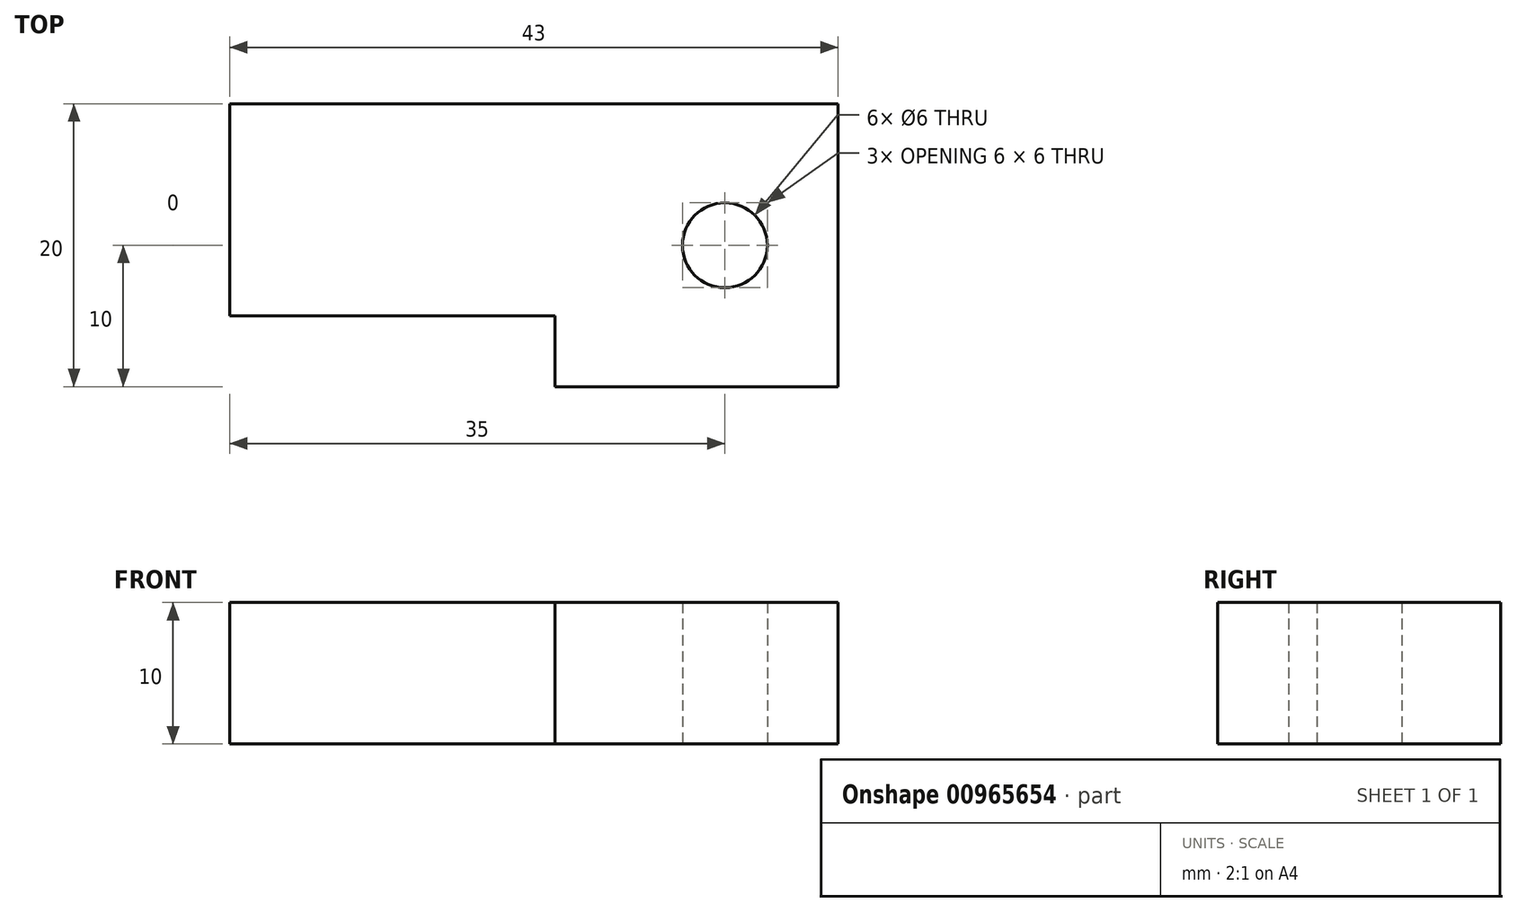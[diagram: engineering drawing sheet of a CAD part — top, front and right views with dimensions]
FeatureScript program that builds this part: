
annotation { "Feature Type Name" : "Feature", "Feature Type Description" : "" }
export const myFeature = defineFeature(function(context is Context, id is Id, definition is map)
    precondition{}
    {
        {
            var Q0;
            Q0=qCreatedBy(makeId("Top.planeOp"),FACE);
            var sketch = newSketch(context, id + "F0", { "sketchPlane" : qUnion([Q0])});
            skLineSegment(sketch, "E0.bottom", {"start": v(21.5, -10) * mm, "end": v(-21.5, -10) * mm});
            skLineSegment(sketch, "E0.top", {"start": v(21.5, 10) * mm, "end": v(-21.5, 10) * mm});
            skLineSegment(sketch, "E0.left", {"start": v(21.5, -10) * mm, "end": v(21.5, 10) * mm});
            skLineSegment(sketch, "E0.right", {"start": v(-21.5, -10) * mm, "end": v(-21.5, 10) * mm});
            skPoint(sketch, "E0.middle", {"position": v(0, 0) * mm});
            skPoint(sketch, "E1.centerSnap0", {"position": v(21.5, 0) * mm});
            skPoint(sketch, "E2", {"position": v(13.5, 0) * mm});
            skSolve(sketch);
        }
        {
            var Q0;
            Q0 = qSketchRegion(id + "F0", true);
            extrude(context, id + "F1", {"entities" : qUnion([Q0]), "depth" : 10 * mm, "offsetDistance" : 25 * mm});
        }
        {
            var Q0;
            Q0=sQuery(id+"F0.wireOp",VERTEX,"E2");
            var Q1;
            Q1=makeQuery(id+"F1.opExtrude","SWEPT_BODY",BODY,{"disambiguationData":[OSD([sQuery(id+"F0.wireOp",EDGE,"E0.bottom"),sQuery(id+"F0.wireOp",EDGE,"E0.top"),sQuery(id+"F0.wireOp",EDGE,"E0.left"),sQuery(id+"F0.wireOp",EDGE,"E0.right")])]});
            hole(context, id + "F2", {"style" : HoleStyle.SIMPLE, "endStyle" : HoleEndStyle.THROUGH, "oppositeDirection" : true, "holeDiameter" : 6 * mm, "majorDiameter" : 5 * mm, "isTappedThrough" : true, "tappedDepth" : 12 * mm, "tapClearance" : 3, "locations" : qUnion([Q0]), "scope" : qUnion([Q1])});
        }
        {
            var Q0;
            Q0=makeQuery(id+"F1.opExtrude","CAP_FACE",FACE,{"disambiguationData":[OSD([sQuery(id+"F0.wireOp",EDGE,"E0.bottom"),sQuery(id+"F0.wireOp",EDGE,"E0.top"),sQuery(id+"F0.wireOp",EDGE,"E0.left"),sQuery(id+"F0.wireOp",EDGE,"E0.right")])],"isStart":true});
            var sketch = newSketch(context, id + "F3", { "sketchPlane" : qUnion([Q0])});
            skLineSegment(sketch, "E3.bottom", {"start": v(-21.5, 10) * mm, "end": v(1.5, 10) * mm});
            skLineSegment(sketch, "E3.top", {"start": v(-21.5, 5) * mm, "end": v(1.5, 5) * mm});
            skLineSegment(sketch, "E3.left", {"start": v(-21.5, 10) * mm, "end": v(-21.5, 5) * mm});
            skLineSegment(sketch, "E3.right", {"start": v(1.5, 10) * mm, "end": v(1.5, 5) * mm});
            skSolve(sketch);
        }
        {
            var Q0;
            Q0=makeQuery(id+"F3.imprint","IMPRINT",FACE,{"disambiguationData":[TD([[makeQuery(id+"F3.imprint","IMPRINT",EDGE,{"derivedFrom":sQuery(id+"F3.wireOp",EDGE,"E3.bottom")}),1.0]])]});
            extrude(context, id + "F4", {"entities" : qUnion([Q0]), "operationType" : NewBodyOperationType.REMOVE, "oppositeDirection" : true, "depth" : 10 * mm, "offsetDistance" : 25 * mm});
        }
    });
